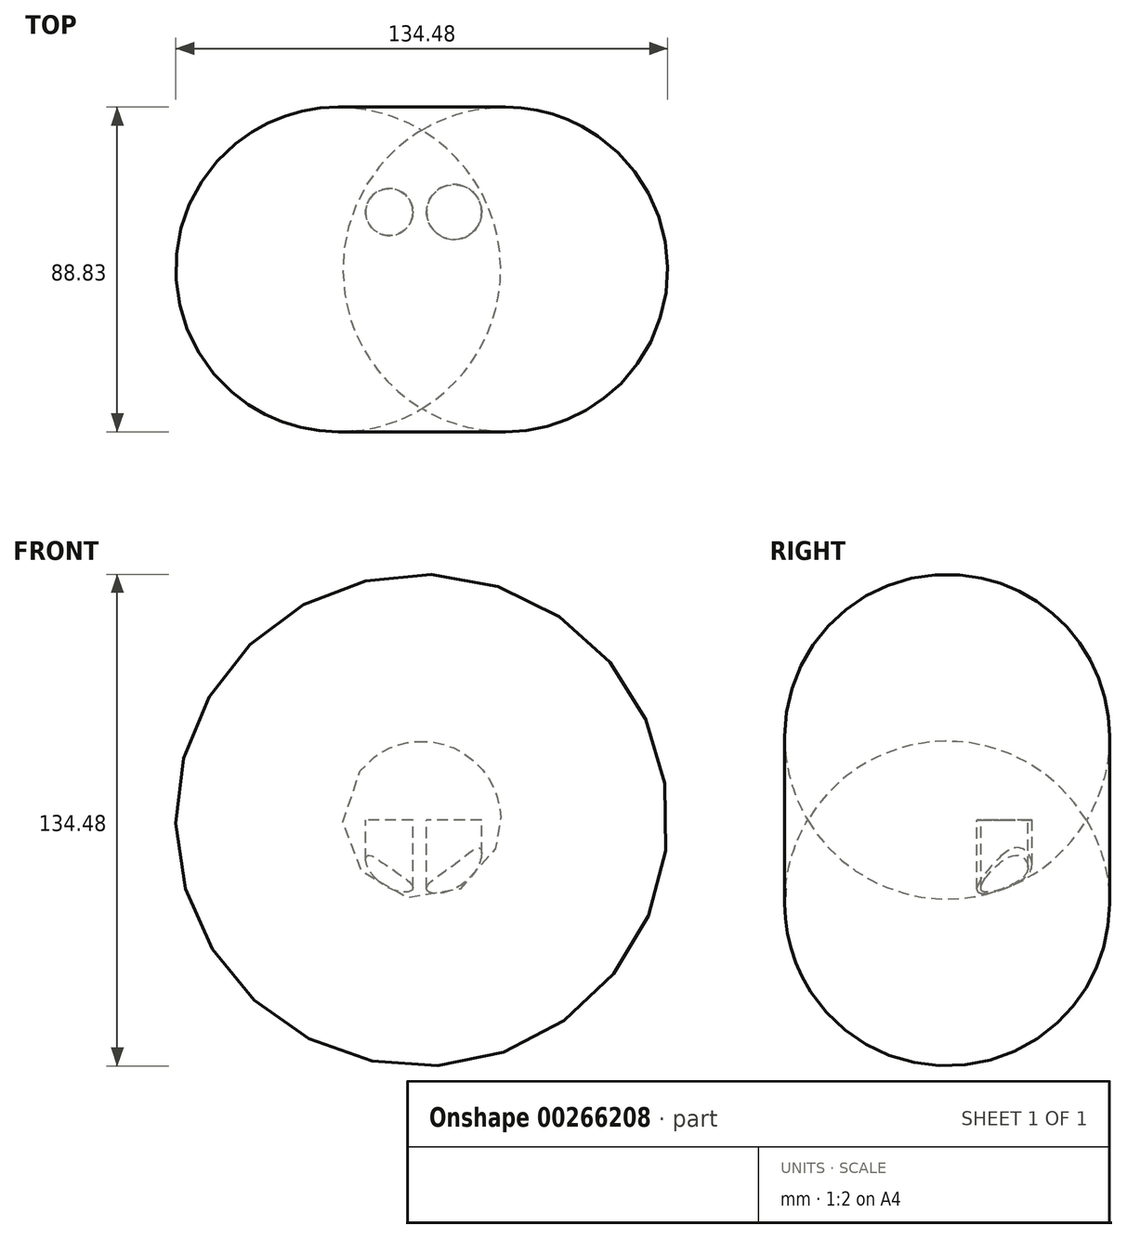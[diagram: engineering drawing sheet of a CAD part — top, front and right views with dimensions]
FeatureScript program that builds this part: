
annotation { "Feature Type Name" : "Feature", "Feature Type Description" : "" }
export const myFeature = defineFeature(function(context is Context, id is Id, definition is map)
    precondition{}
    {
        {
            var Q0;
            Q0=qCreatedBy(makeId("Top.planeOp"),FACE);
            var sketch = newSketch(context, id + "F0", { "sketchPlane" : qUnion([Q0])});
            skLineSegment(sketch, "E0", {"start": v(0, 42.3) * mm, "end": v(0, -33.9) * mm, "construction": true});
            skLineSegment(sketch, "E1", {"start": v(0, 42.3) * mm, "end": v(0, -33.9) * mm});
            skArc(sketch, "E2", {"start": v(0, 42.3) * mm, "mid": v(-21.59, 4.2) * mm, "end": v(0, -33.9) * mm});
            skSolve(sketch);
        }
        {
            var Q0;
            Q0=makeQuery(id+"F0.imprint","IMPRINT",FACE,{"disambiguationData":[TD([[makeQuery(id+"F0.imprint","IMPRINT",EDGE,{"derivedFrom":sQuery(id+"F0.wireOp",EDGE,"E1")}),-1.0]])]});
            var Q1;
            Q1=sQuery(id+"F0.wireOp",EDGE,"E1");
            revolve(context, id + "F1", {"entities" : qUnion([Q0]), "axis" : qUnion([Q1]), "revolveType" : RevolveType.FULL});
        }
        {
            var Q0;
            Q0=qCreatedBy(makeId("Top.planeOp"),FACE);
            var sketch = newSketch(context, id + "F2", { "sketchPlane" : qUnion([Q0])});
            skCircle(sketch, "E3", {"center": v(-8.88, 19.9) * mm, "radius": 6.45 * mm});
            skCircle(sketch, "E4", {"center": v(8.86, 19.9) * mm, "radius": 7.52 * mm});
            skSolve(sketch);
        }
        {
            var Q0;
            Q0 = qSketchRegion(id + "F2", true);
            extrude(context, id + "F3", {"entities" : qUnion([Q0]), "operationType" : NewBodyOperationType.REMOVE, "oppositeDirection" : true, "depth" : 25.4 * mm});
        }
    });
